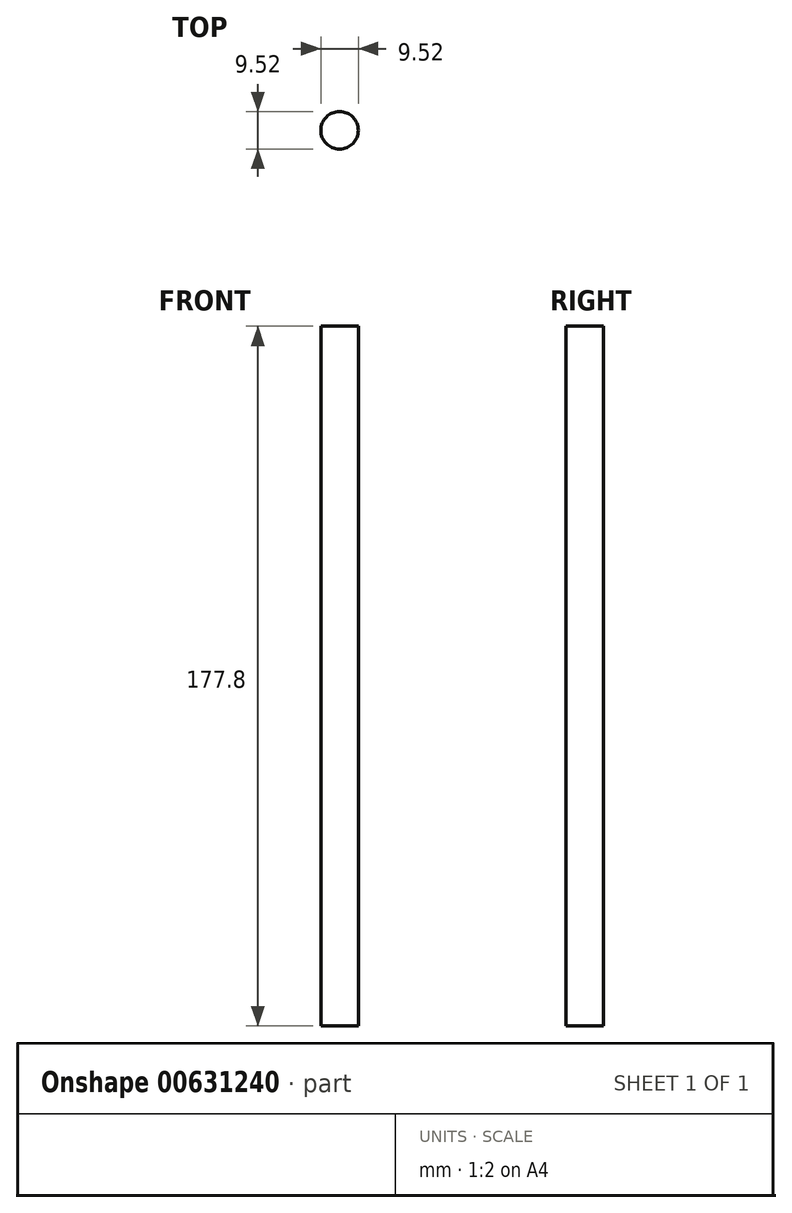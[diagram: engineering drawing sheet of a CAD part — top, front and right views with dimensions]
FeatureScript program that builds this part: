
annotation { "Feature Type Name" : "Feature", "Feature Type Description" : "" }
export const myFeature = defineFeature(function(context is Context, id is Id, definition is map)
    precondition{}
    {
        {
            var Q0;
            Q0=qCreatedBy(makeId("Top.planeOp"),FACE);
            var sketch = newSketch(context, id + "F0", { "sketchPlane" : qUnion([Q0])});
            skCircle(sketch, "E0", {"center": v(0, 0) * mm, "radius": 4.76 * mm});
            skSolve(sketch);
        }
        {
            var Q0;
            Q0 = qSketchRegion(id + "F0", true);
            extrude(context, id + "F1", {"entities" : qUnion([Q0]), "depth" : 177.8 * mm, "offsetDistance" : 25.4 * mm});
        }
    });
